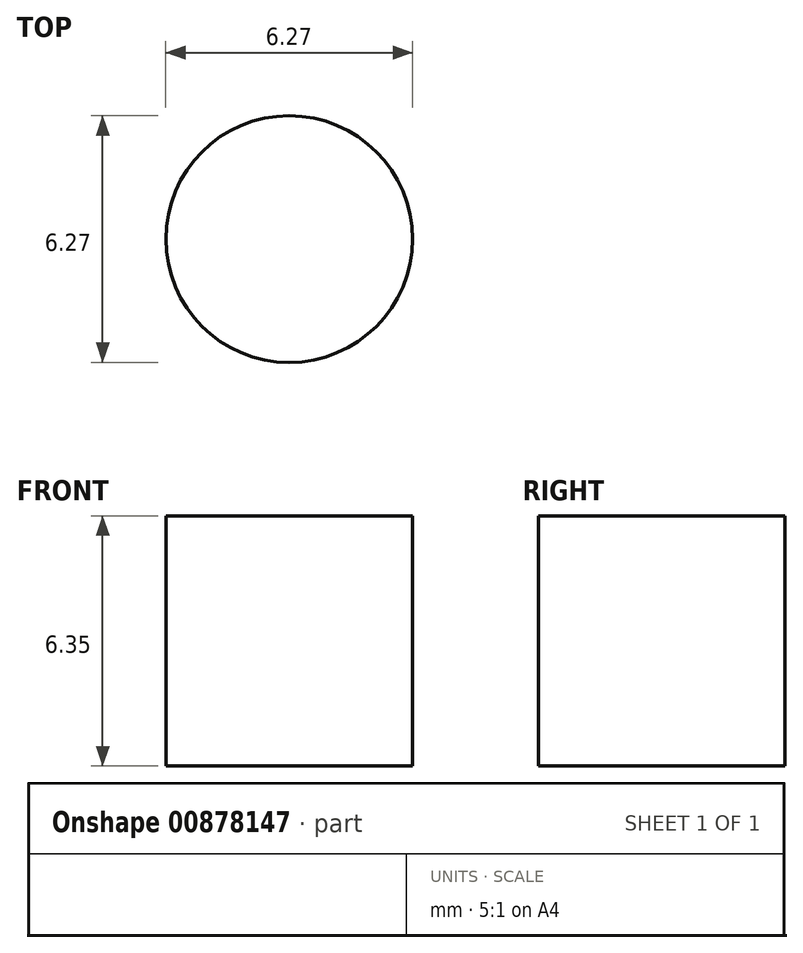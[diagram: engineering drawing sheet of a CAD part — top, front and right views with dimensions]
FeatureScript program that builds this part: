
annotation { "Feature Type Name" : "Feature", "Feature Type Description" : "" }
export const myFeature = defineFeature(function(context is Context, id is Id, definition is map)
    precondition{}
    {
        {
            var Q0;
            Q0=qCreatedBy(makeId("Top.planeOp"),FACE);
            var sketch = newSketch(context, id + "F0", { "sketchPlane" : qUnion([Q0])});
            skCircle(sketch, "E0", {"center": v(-63.35, 26.44) * mm, "radius": 3.13 * mm});
            skSolve(sketch);
        }
        {
            var Q0;
            Q0=makeQuery(id+"F0.imprint","IMPRINT",FACE,{"disambiguationData":[TD([[makeQuery(id+"F0.imprint","IMPRINT",EDGE,{"derivedFrom":sQuery(id+"F0.wireOp",EDGE,"E0")}),1.0]])]});
            extrude(context, id + "F1", {"entities" : qUnion([Q0]), "depth" : 6.35 * mm, "offsetDistance" : 25.4 * mm});
        }
    });
